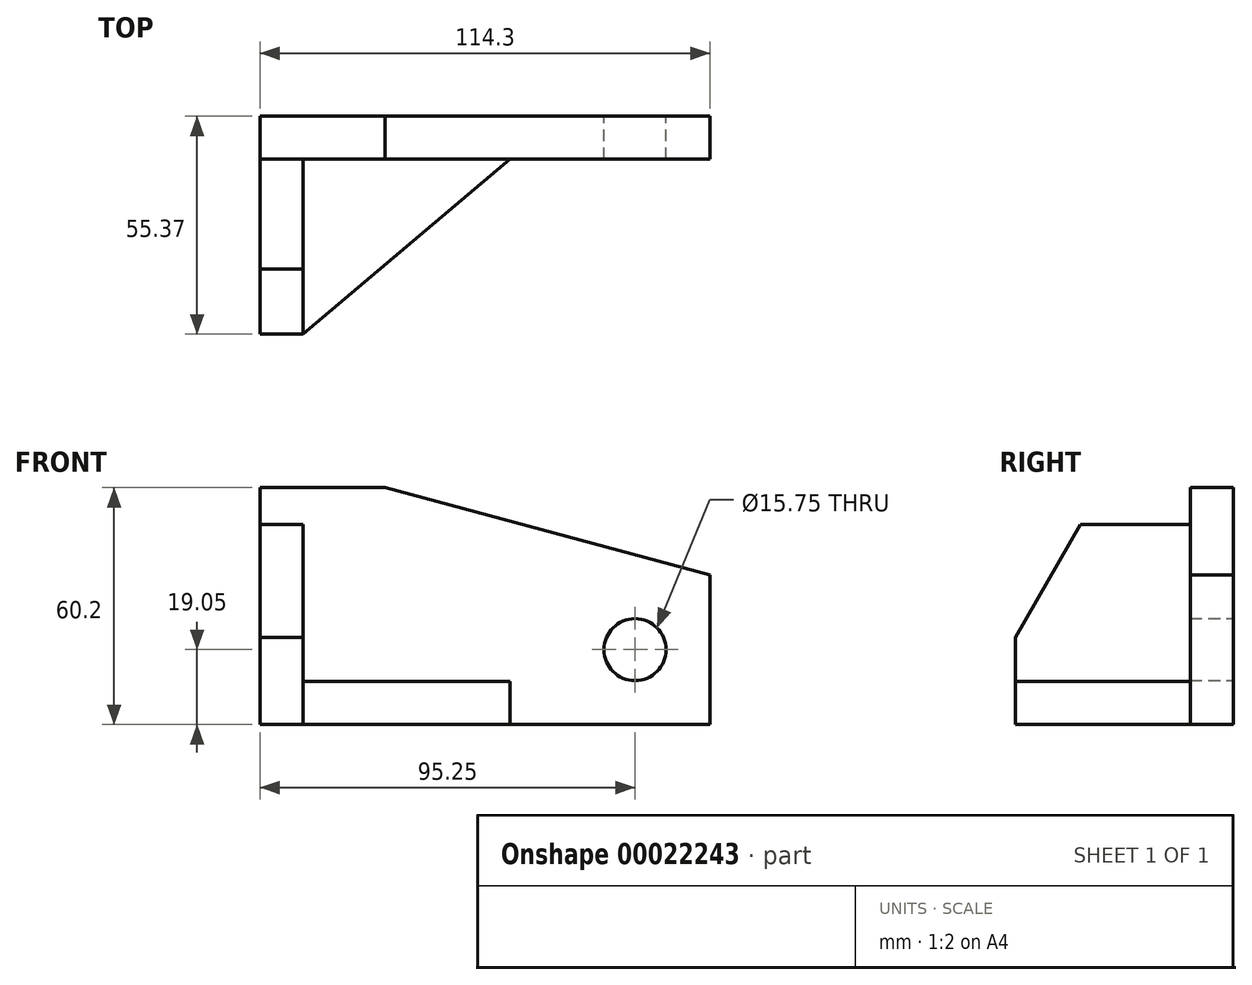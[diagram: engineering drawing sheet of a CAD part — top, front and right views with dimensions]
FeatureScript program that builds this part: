
annotation { "Feature Type Name" : "Feature", "Feature Type Description" : "" }
export const myFeature = defineFeature(function(context is Context, id is Id, definition is map)
    precondition{}
    {
        {
            var Q0;
            Q0=qCreatedBy(makeId("Front.planeOp"),FACE);
            var sketch = newSketch(context, id + "F0", { "sketchPlane" : qUnion([Q0])});
            skLineSegment(sketch, "E0.bottom", {"start": v(0, 0) * mm, "end": v(-114.3, 0) * mm});
            skLineSegment(sketch, "E0.top", {"start": v(-82.55, 60.2) * mm, "end": v(-114.3, 60.2) * mm});
            skLineSegment(sketch, "E0.left", {"start": v(0, 0) * mm, "end": v(0, 38.08) * mm});
            skLineSegment(sketch, "E0.right", {"start": v(-114.3, 0) * mm, "end": v(-114.3, 60.2) * mm});
            skLineSegment(sketch, "E1", {"start": v(-114.3, 60.2) * mm, "end": v(-82.55, 60.2) * mm});
            skLineSegment(sketch, "E2", {"start": v(-82.55, 60.2) * mm, "end": v(0, 38.08) * mm});
            skPoint(sketch, "E3.orphan", {"position": v(0, 60.2) * mm});
            skLineSegment(sketch, "E4", {"start": v(0, 0) * mm, "end": v(0, 0) * mm});
            skCircle(sketch, "E5", {"center": v(-19.05, 19.05) * mm, "radius": 7.87 * mm});
            skSolve(sketch);
        }
        {
            var Q0;
            Q0 = qSketchRegion(id + "F0", true);
            extrude(context, id + "F1", {"entities" : qUnion([Q0]), "depth" : 10.92 * mm});
        }
        {
            var Q0;
            Q0=makeQuery(id+"F1.opExtrude","SWEPT_FACE",FACE,{"disambiguationData":[OSD([sQuery(id+"F0.wireOp",EDGE,"E0.right")])]});
            var sketch = newSketch(context, id + "F2", { "sketchPlane" : qUnion([Q0])});
            skLineSegment(sketch, "E6.bottom", {"start": v(10.92, 0) * mm, "end": v(55.37, 0) * mm});
            skLineSegment(sketch, "E6.top", {"start": v(10.92, 50.8) * mm, "end": v(38.8, 50.8) * mm});
            skLineSegment(sketch, "E6.left", {"start": v(10.92, 0) * mm, "end": v(10.92, 50.8) * mm});
            skLineSegment(sketch, "E6.right", {"start": v(55.37, 0) * mm, "end": v(55.37, 22.1) * mm});
            skLineSegment(sketch, "E7", {"start": v(55.37, 22.1) * mm, "end": v(38.8, 50.8) * mm});
            skPoint(sketch, "E8.orphan", {"position": v(55.37, 50.8) * mm});
            skSolve(sketch);
        }
        {
            var Q0;
            Q0=makeQuery(id+"F2.imprint","IMPRINT",FACE,{"disambiguationData":[TD([[makeQuery(id+"F2.imprint","IMPRINT",EDGE,{"derivedFrom":sQuery(id+"F2.wireOp",EDGE,"E6.bottom")}),1.0]])]});
            extrude(context, id + "F3", {"entities" : qUnion([Q0]), "oppositeDirection" : true, "depth" : 10.92 * mm});
        }
        {
            var Q0;
            Q0=makeQuery(id+"F3.opExtrude","SWEPT_FACE",FACE,{"disambiguationData":[OSD([sQuery(id+"F2.wireOp",EDGE,"E6.bottom")])]});
            var sketch = newSketch(context, id + "F4", { "sketchPlane" : qUnion([Q0])});
            skLineSegment(sketch, "E9.bottom", {"start": v(-103.38, 10.92) * mm, "end": v(-50.8, 10.92) * mm});
            skLineSegment(sketch, "E9.left", {"start": v(-103.38, 10.92) * mm, "end": v(-103.38, 55.37) * mm});
            skLineSegment(sketch, "E10", {"start": v(-103.38, 55.37) * mm, "end": v(-50.8, 10.92) * mm});
            skPoint(sketch, "E9.right.end.orphan", {"position": v(-39.88, 55.37) * mm});
            skSolve(sketch);
        }
        {
            var Q0;
            Q0=makeQuery(id+"F4.imprint","IMPRINT",FACE,{"disambiguationData":[TD([[makeQuery(id+"F4.imprint","IMPRINT",EDGE,{"derivedFrom":sQuery(id+"F4.wireOp",EDGE,"E9.bottom")}),1.0]])]});
            extrude(context, id + "F5", {"entities" : qUnion([Q0]), "oppositeDirection" : true, "depth" : 10.92 * mm});
        }
    });
